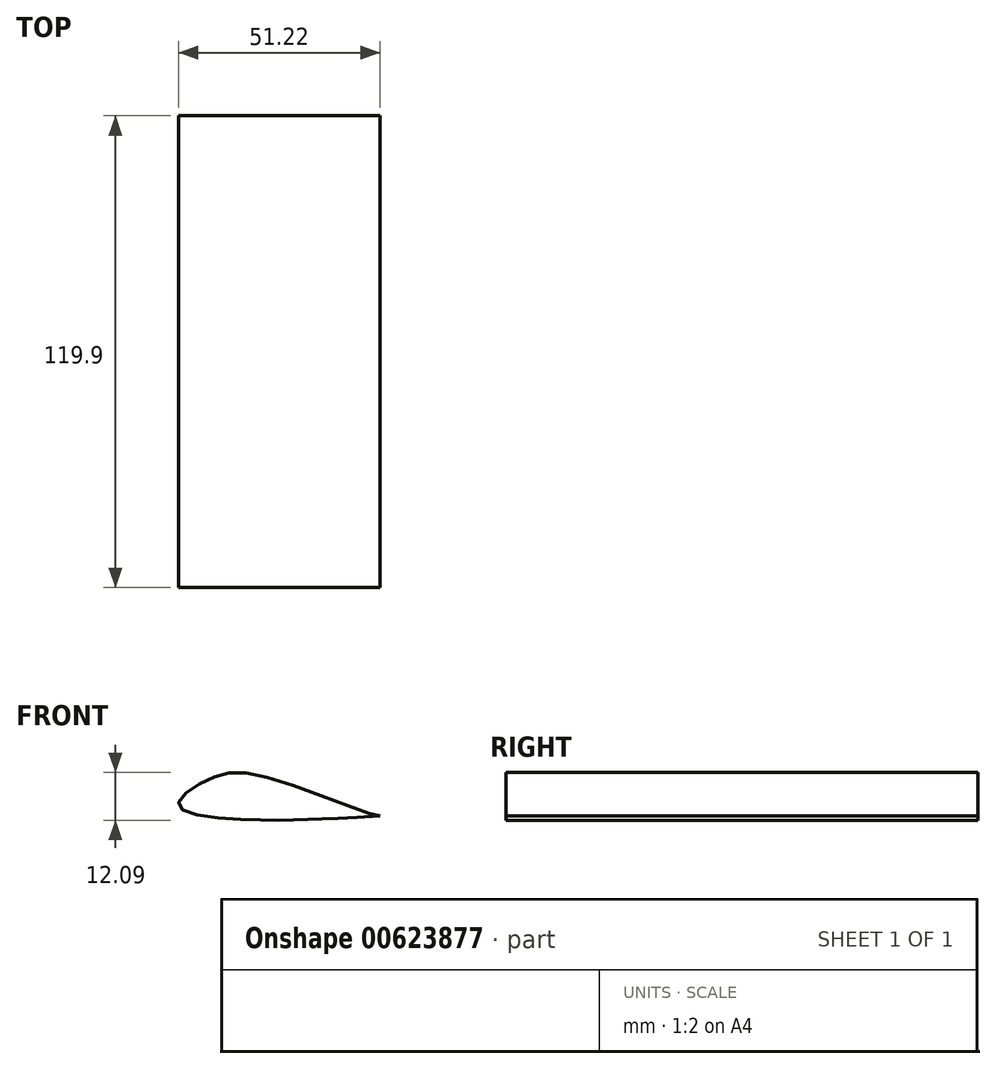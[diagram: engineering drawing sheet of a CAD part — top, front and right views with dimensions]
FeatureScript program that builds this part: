
annotation { "Feature Type Name" : "Feature", "Feature Type Description" : "" }
export const myFeature = defineFeature(function(context is Context, id is Id, definition is map)
    precondition{}
    {
        {
            var Q0;
            Q0=qCreatedBy(makeId("Front.planeOp"),FACE);
            var sketch = newSketch(context, id + "F0", { "sketchPlane" : qUnion([Q0])});
            skFitSpline(sketch, "E0", {"points": [v(-22.37, 0) * mm, v(-15.49, 6.27) * mm, v(0, 7.13) * mm, v(28.77, -2.7) * mm, v(29.17, -1.86) * mm, v(37.1, 2.54) * mm, v(41.38, 0) * mm, v(23.17, -3.08) * mm, v(9.24, -3.62) * mm, v(-6.3, -3.62) * mm, v(-22.37, 0) * mm]});
            skLineSegment(sketch, "E1", {"start": v(21.69, 14.75) * mm, "end": v(32.57, -12.03) * mm});
            skSolve(sketch);
        }
        {
            var Q0;
            {var subQ0=sQuery(id+"F0.wireOp",EDGE,"E1");var subQ1=sQuery(id+"F0.wireOp",EDGE,"E0");var subQ2=makeQuery(id+"F0.imprint","INTERSECT",VERTEX,{"disambiguationData":[OD(0.0)],"derivedFrom":[subQ1,subQ0]});Q0=makeQuery(id+"F0.imprint","IMPRINT",FACE,{"disambiguationData":[TD([[makeQuery(id+"F0.imprint","IMPRINT",EDGE,{"disambiguationData":[TD([[subQ2,1.0]])],"derivedFrom":subQ1}),-1.0]])]});}
            extrude(context, id + "F1", {"entities" : qUnion([Q0]), "depth" : 119.9 * mm, "offsetDistance" : 25 * mm});
        }
    });
